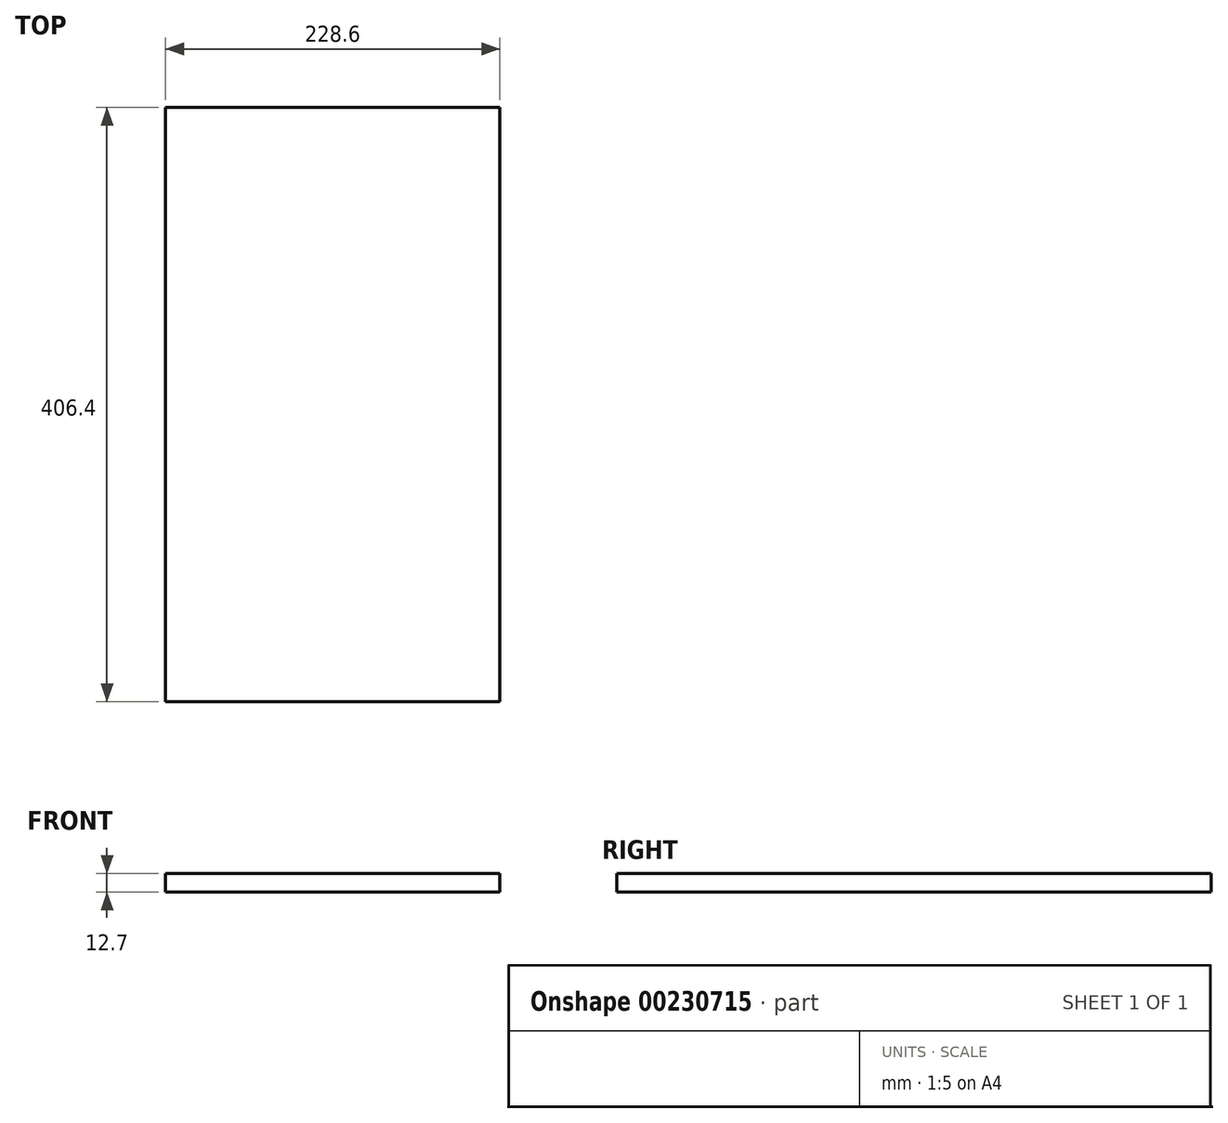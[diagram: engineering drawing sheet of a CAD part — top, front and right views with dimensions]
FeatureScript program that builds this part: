
annotation { "Feature Type Name" : "Feature", "Feature Type Description" : "" }
export const myFeature = defineFeature(function(context is Context, id is Id, definition is map)
    precondition{}
    {
        {
            var Q0;
            Q0=qCreatedBy(makeId("Front.planeOp"),FACE);
            var sketch = newSketch(context, id + "F0", { "sketchPlane" : qUnion([Q0])});
            skLineSegment(sketch, "E0.bottom", {"start": v(-119.13, -2.27) * mm, "end": v(109.47, -2.27) * mm});
            skLineSegment(sketch, "E0.top", {"start": v(-119.13, -14.97) * mm, "end": v(109.47, -14.97) * mm});
            skLineSegment(sketch, "E0.left", {"start": v(-119.13, -2.27) * mm, "end": v(-119.13, -14.97) * mm});
            skLineSegment(sketch, "E0.right", {"start": v(109.47, -2.27) * mm, "end": v(109.47, -14.97) * mm});
            skSolve(sketch);
        }
        {
            var Q0;
            Q0=makeQuery(id+"F0.imprint","IMPRINT",FACE,{"disambiguationData":[TD([[makeQuery(id+"F0.imprint","IMPRINT",EDGE,{"derivedFrom":sQuery(id+"F0.wireOp",EDGE,"E0.bottom")}),-1.0]])]});
            extrude(context, id + "F1", {"entities" : qUnion([Q0]), "oppositeDirection" : true, "depth" : 406.4 * mm});
        }
    });
